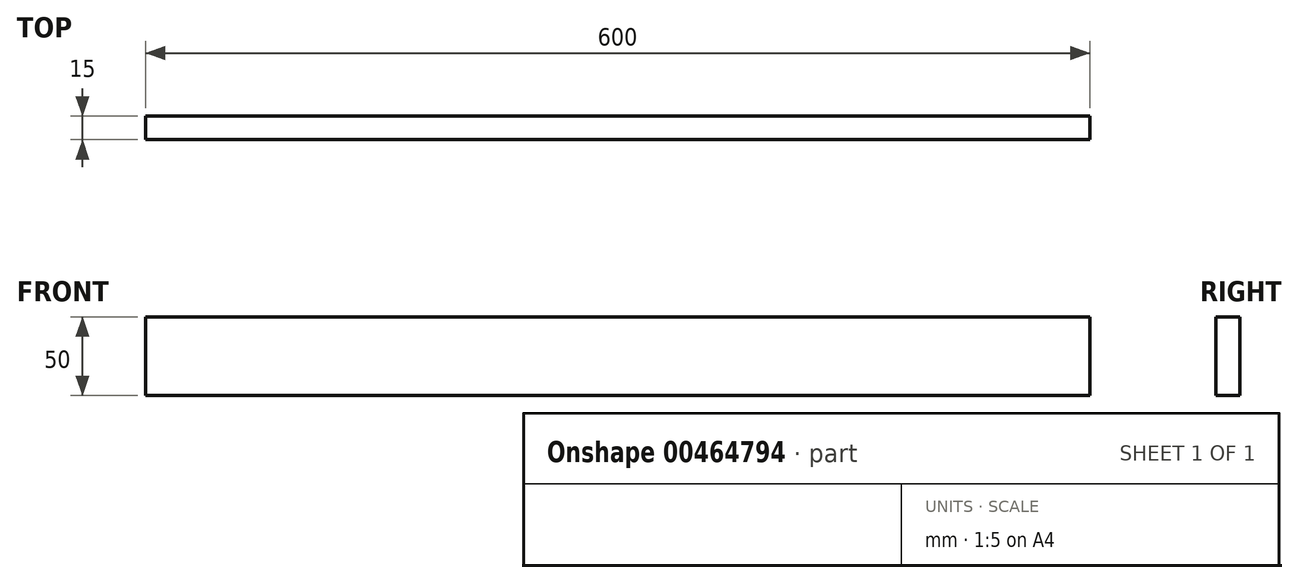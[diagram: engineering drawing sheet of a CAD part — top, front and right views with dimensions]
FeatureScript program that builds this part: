
annotation { "Feature Type Name" : "Feature", "Feature Type Description" : "" }
export const myFeature = defineFeature(function(context is Context, id is Id, definition is map)
    precondition{}
    {
        {
            var Q0;
            Q0=qCreatedBy(makeId("Front.planeOp"),FACE);
            var sketch = newSketch(context, id + "F0", { "sketchPlane" : qUnion([Q0])});
            skLineSegment(sketch, "E0.bottom", {"start": v(0, 0) * mm, "end": v(600, 0) * mm});
            skLineSegment(sketch, "E0.top", {"start": v(0, 50) * mm, "end": v(600, 50) * mm});
            skLineSegment(sketch, "E0.left", {"start": v(0, 0) * mm, "end": v(0, 50) * mm});
            skLineSegment(sketch, "E0.right", {"start": v(600, 0) * mm, "end": v(600, 50) * mm});
            skSolve(sketch);
        }
        {
            var Q0;
            Q0 = qSketchRegion(id + "F0", true);
            extrude(context, id + "F1", {"entities" : qUnion([Q0]), "depth" : 15 * mm});
        }
    });
